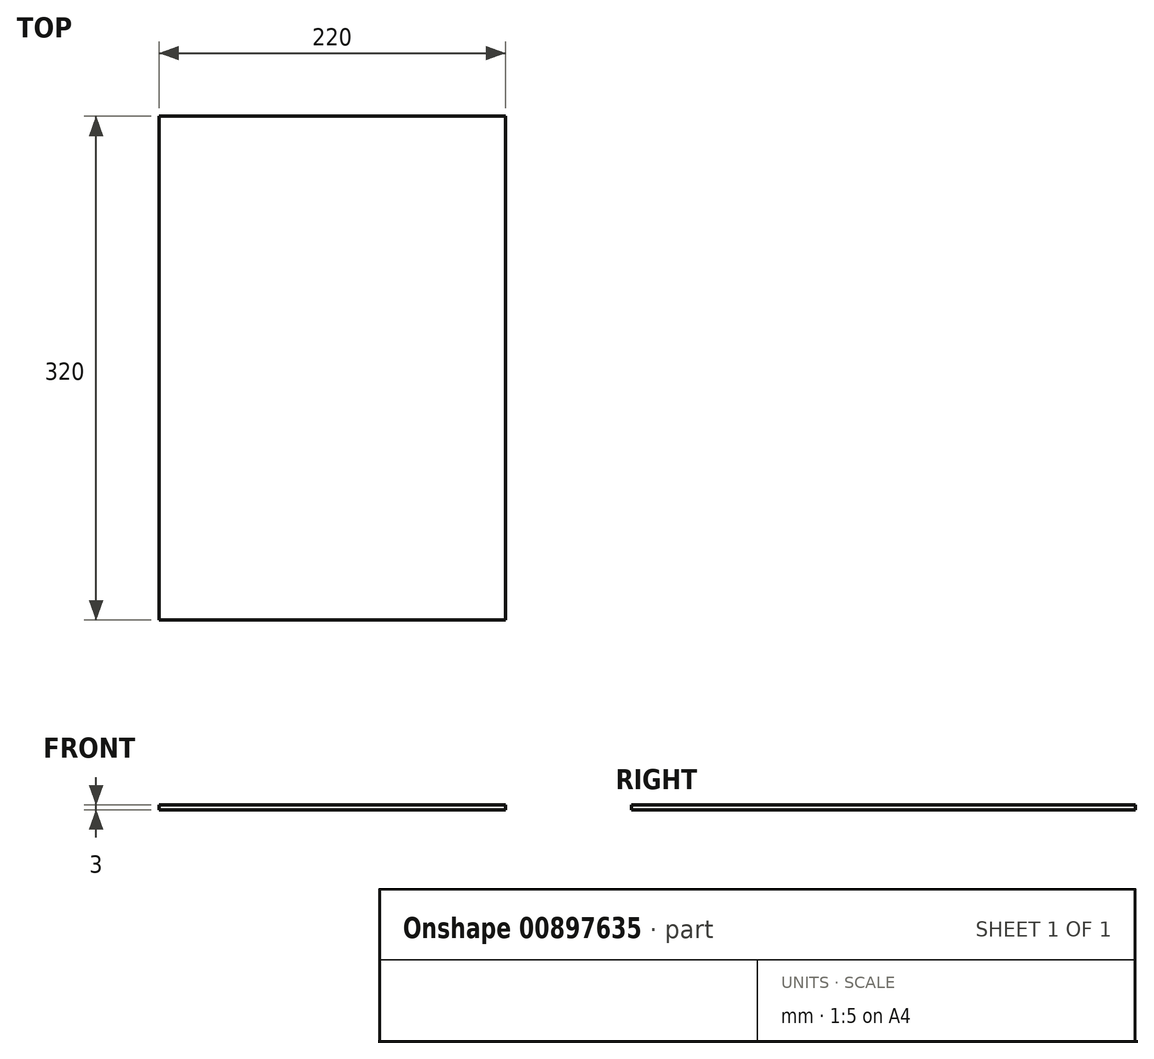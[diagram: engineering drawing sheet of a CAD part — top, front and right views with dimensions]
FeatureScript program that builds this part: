
annotation { "Feature Type Name" : "Feature", "Feature Type Description" : "" }
export const myFeature = defineFeature(function(context is Context, id is Id, definition is map)
    precondition{}
    {
        {
            var Q0;
            Q0=qCreatedBy(makeId("Top.planeOp"),FACE);
            var sketch = newSketch(context, id + "F0", { "sketchPlane" : qUnion([Q0])});
            skLineSegment(sketch, "E0.bottom", {"start": v(0, 0) * mm, "end": v(220, 0) * mm});
            skLineSegment(sketch, "E0.top", {"start": v(0, 320) * mm, "end": v(220, 320) * mm});
            skLineSegment(sketch, "E0.left", {"start": v(0, 0) * mm, "end": v(0, 320) * mm});
            skLineSegment(sketch, "E0.right", {"start": v(220, 0) * mm, "end": v(220, 320) * mm});
            skSolve(sketch);
        }
        {
            var Q0;
            Q0=makeQuery(id+"F0.imprint","IMPRINT",FACE,{"disambiguationData":[TD([[makeQuery(id+"F0.imprint","IMPRINT",EDGE,{"derivedFrom":sQuery(id+"F0.wireOp",EDGE,"E0.bottom")}),1.0]])]});
            extrude(context, id + "F1", {"entities" : qUnion([Q0]), "depth" : 3 * mm, "offsetDistance" : 25 * mm});
        }
    });
